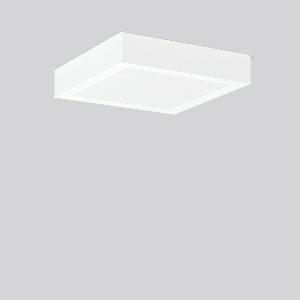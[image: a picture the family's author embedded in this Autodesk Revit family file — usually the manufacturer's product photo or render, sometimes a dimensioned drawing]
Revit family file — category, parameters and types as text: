
# Revit family: toledo_flat_square_a_672278_002_1_07_e7c5
name_source: partatom
category: Lighting Fixtures
units: mm (PartAtom-declared; Revit-internal decimal feet)

## family parameters
Cut with Voids When Loaded = No
Host = Face
Light Source = No
Part Type = Normal
Room Calculation Point = No
Round Connector Dimension = Use Diameter
Shared = No

## types (1)
- TOLEDO FLAT square A (1 x LED Modul 840, 2200 lm, 4000)
    Apparent Load = 25 VA
    CIE Flux Codes = 49 80 96 100 100
    Color Rendering = 80
    Color Temperature = 4000
    Default Elevation = 1800 mm
    Description = Series: TOLEDO FLAT square
Ultra thin surface mounted downlight. For escape route illumination. Surface mounted housing: sheet steel, powder-coated. Square cover plate: die-cast aluminium, powder coated. Light guide and diffuser made of non-yellowing PMMA, opal matt. Self-contained system with automatic self-test and feedback via DALI bus, only to RZB DALI monitoring system. 
Colour: white
Length: 300 mm
Width: 300 mm
Height: 58 mm
Weight: 3.96 kg
Operating mode: maintained power mode
Duration time: 8 h
Lamp: LED
Socket: without socket
Colour temperature: 4000K
Colour rendering index (CRI): 80
System power: 25 W
Rated luminous flux: 2200 lm
Luminous flux, emergency: 180 lm
System power, emergency: -
Control gear: Regulated power supply
Protection class: I
Type of protection: IP 40
    Height = 58 mm
    Lamp = 1 x LED Modul 840
    Lamp Light Flux = 2200 lm
    Lamp count = 1
    Length = 300 mm
    Lifetime = 50000 h
    Luminous efficacy = 88 lm/W
    Manufacturer = RZB
    ModVariant = No
    Model = 672278.002.1.07
    Mounting Place = Ceiling
    Mounting Type = Surface mounted
    Number of Poles = 1
    OnlyDefault = Yes
    Power Factor = 1
    Product Name = TOLEDO FLAT square A
    Product group = Surface mounted downlights
    ProductGroupID = 302
    Protection Class = Protection class I
    Protection Degree = IP 40
    RLX_Detail_Level = 1
    RLX_Emergency_Light_Flux = 180 lm
    RLX_Emergency_Type = 3
    RLX_Emergency_Type_DB = Yes
    RlxData = <blob elided: 14101 chars, md5=11f9728a>
    Socket = socket
    Standby Power = 0 W
    System Light Flux = 2200 lm
    System Power = 25 W
    Type Comments = Product without accessories
    Type Image = 901554.002.jpg
    URL = http://relux.com
    VarID = ---
    Voltage = 0 V
    Weight = 0.00 kg
    Width = 300 mm

## geometry (parser evidence)
native form markers: Sweep x12
no freeform markers — native parametric forms only
